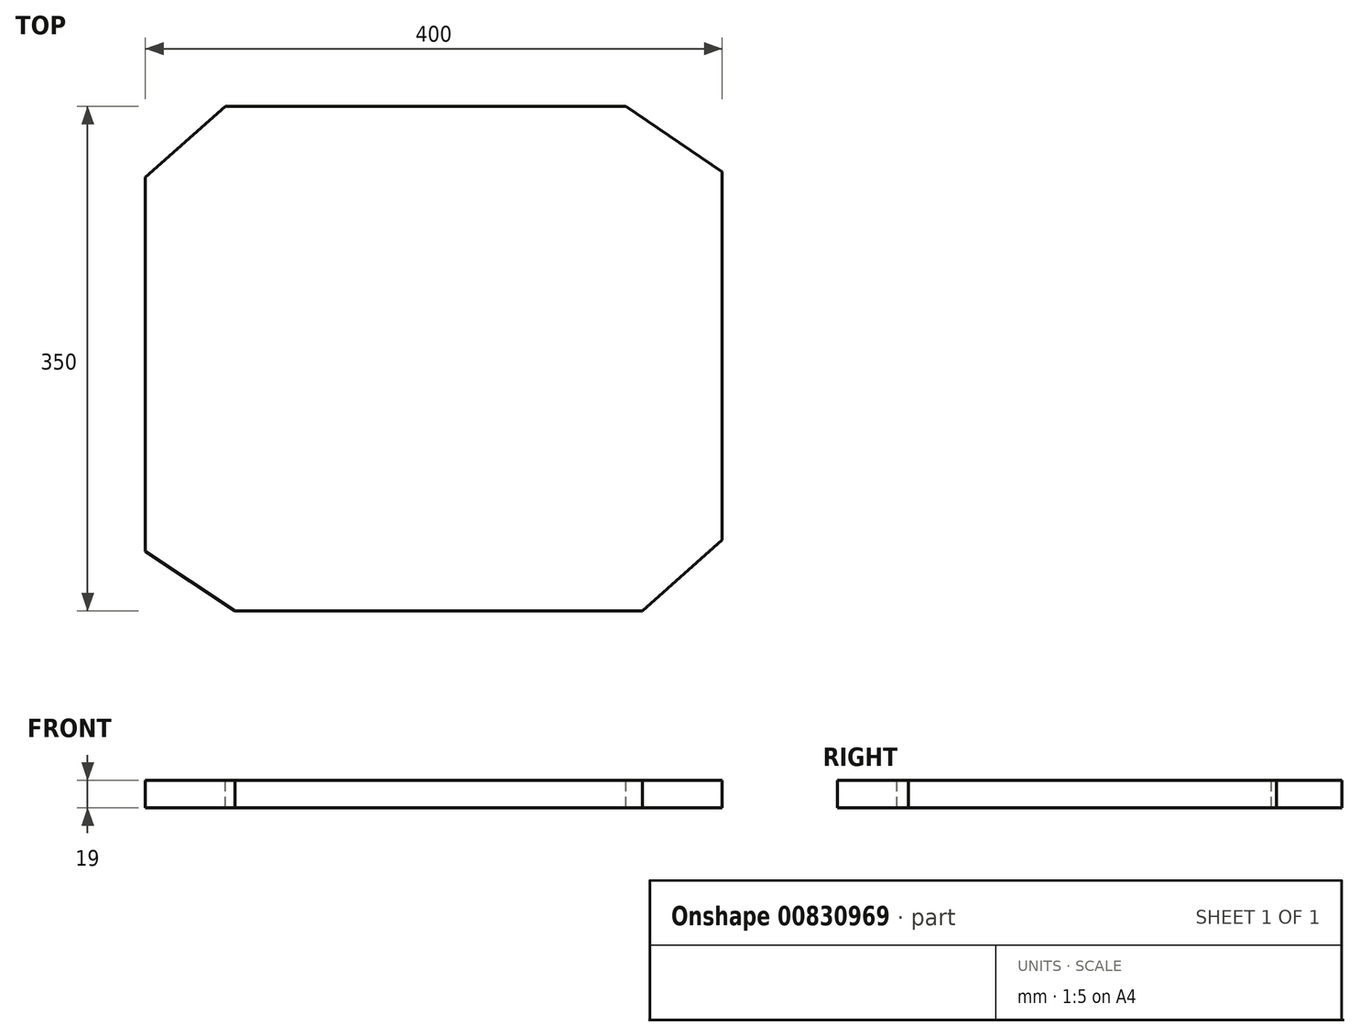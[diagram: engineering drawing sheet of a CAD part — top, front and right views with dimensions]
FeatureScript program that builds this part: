
annotation { "Feature Type Name" : "Feature", "Feature Type Description" : "" }
export const myFeature = defineFeature(function(context is Context, id is Id, definition is map)
    precondition{}
    {
        {
            var Q0;
            Q0=qCreatedBy(makeId("Top.planeOp"),FACE);
            var sketch = newSketch(context, id + "F0", { "sketchPlane" : qUnion([Q0])});
            skLineSegment(sketch, "E0.bottom", {"start": v(-200, -175) * mm, "end": v(200, -175) * mm});
            skLineSegment(sketch, "E0.top", {"start": v(-200, 175) * mm, "end": v(200, 175) * mm});
            skLineSegment(sketch, "E0.left", {"start": v(-200, -175) * mm, "end": v(-200, 175) * mm});
            skLineSegment(sketch, "E0.right", {"start": v(200, -175) * mm, "end": v(200, 175) * mm});
            skPoint(sketch, "E0.middle", {"position": v(0, 0) * mm});
            skSolve(sketch);
        }
        {
            var Q0;
            Q0=makeQuery(id+"F0.imprint","IMPRINT",FACE,{"disambiguationData":[TD([[makeQuery(id+"F0.imprint","IMPRINT",EDGE,{"derivedFrom":sQuery(id+"F0.wireOp",EDGE,"E0.bottom")}),1.0]])]});
            extrude(context, id + "F1", {"entities" : qUnion([Q0]), "depth" : 19 * mm, "offsetDistance" : 25 * mm});
        }
        {
            var Q0;
            Q0=makeQuery(id+"F1.opExtrude","CAP_FACE",FACE,{"disambiguationData":[OSD([sQuery(id+"F0.wireOp",EDGE,"E0.bottom"),sQuery(id+"F0.wireOp",EDGE,"E0.top"),sQuery(id+"F0.wireOp",EDGE,"E0.left"),sQuery(id+"F0.wireOp",EDGE,"E0.right")])],"isStart":false});
            var sketch = newSketch(context, id + "F2", { "sketchPlane" : qUnion([Q0])});
            skLineSegment(sketch, "E1", {"start": v(-200, -133.68) * mm, "end": v(-137.88, -175) * mm});
            skLineSegment(sketch, "E2", {"start": v(-137.88, -175) * mm, "end": v(144.7, -175) * mm});
            skLineSegment(sketch, "E3", {"start": v(144.7, -175) * mm, "end": v(200, -125.82) * mm});
            skLineSegment(sketch, "E4", {"start": v(200, -125.82) * mm, "end": v(200, 129.5) * mm});
            skLineSegment(sketch, "E5", {"start": v(200, 129.5) * mm, "end": v(133.16, 175) * mm});
            skLineSegment(sketch, "E6", {"start": v(133.16, 175) * mm, "end": v(-144.7, 175) * mm});
            skLineSegment(sketch, "E7", {"start": v(-144.7, 175) * mm, "end": v(-200, 125.82) * mm});
            skSolve(sketch);
        }
        {
            var Q0;
            {var subQ0=sQuery(id+"F2.wireOp",EDGE,"E7");Q0=makeQuery(id+"F2.imprint","IMPRINT",FACE,{"disambiguationData":[TD([[makeQuery(id+"F2.imprint","IMPRINT",EDGE,{"derivedFrom":subQ0}),-1.0]])]});}
            var Q1;
            {var subQ0=sQuery(id+"F2.wireOp",EDGE,"E3");Q1=makeQuery(id+"F2.imprint","IMPRINT",FACE,{"disambiguationData":[TD([[makeQuery(id+"F2.imprint","IMPRINT",EDGE,{"derivedFrom":subQ0}),-1.0]])]});}
            var Q2;
            {var subQ0=sQuery(id+"F2.wireOp",EDGE,"E1");Q2=makeQuery(id+"F2.imprint","IMPRINT",FACE,{"disambiguationData":[TD([[makeQuery(id+"F2.imprint","IMPRINT",EDGE,{"derivedFrom":subQ0}),-1.0]])]});}
            var Q3;
            {var subQ0=sQuery(id+"F2.wireOp",EDGE,"E5");Q3=makeQuery(id+"F2.imprint","IMPRINT",FACE,{"disambiguationData":[TD([[makeQuery(id+"F2.imprint","IMPRINT",EDGE,{"derivedFrom":subQ0}),-1.0]])]});}
            extrude(context, id + "F3", {"entities" : qUnion([Q0, Q1, Q2, Q3]), "operationType" : NewBodyOperationType.REMOVE, "endBound" : BoundingType.THROUGH_ALL, "oppositeDirection" : true, "depth" : 25 * mm, "offsetDistance" : 25 * mm});
        }
    });
